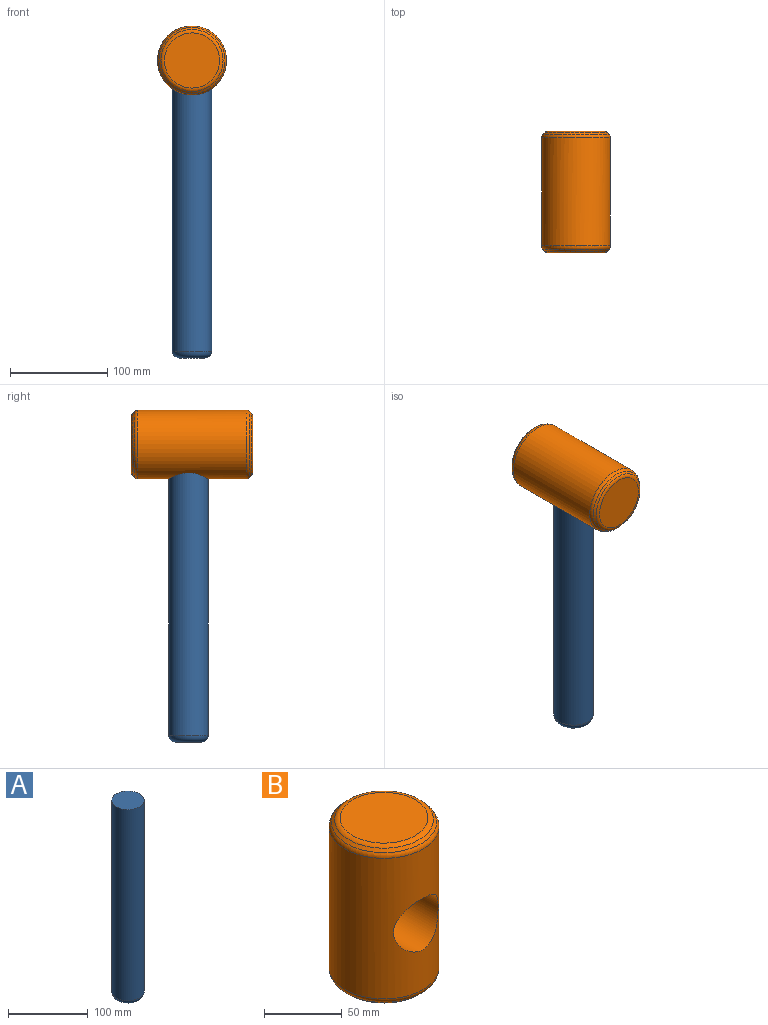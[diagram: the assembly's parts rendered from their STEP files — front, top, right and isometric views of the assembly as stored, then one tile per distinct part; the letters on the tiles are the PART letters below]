
ASSEMBLY  parts=2 mates=1
PART A: 4 faces, bbox 43.7x43.7x300 mm
  f0: cylinder r=20.2mm len=293mm, axis (0,0,-1), area 37190.6mm2, adj f1,f3
  f1: plane 40.4x40.4mm, normal (0,0,1), area 1282.1mm2, adj f0
  f2: plane 26.4x26.4mm, normal (0,0,-1), area 547.5mm2, adj f3
  f3: torus R=13.2mm, axis (0,0,1), area 1219.9mm2, adj f0,f2
PART B: 11 faces, bbox 76.6x76.6x125 mm
  f0: cylinder r=35.39mm len=110.86mm, axis (0,0,-1), area 23300.9mm2, adj f3,f8,f9
  f1: plane 56.64x56.64mm, normal (0,0,-1), area 2519.6mm2, adj f7
  f2: plane 56.64x56.64mm, normal (0,0,1), area 2519.6mm2, adj f10
  f3: cylinder r=20.3mm len=60.39mm, axis (0,1,0), area 7305.7mm2, adj f0,f4
  f4: plane 40.61x40.61mm, normal (0,-1,0), area 1295mm2, adj f3
  f5: cone r=30.39mm half-angle=45deg, axis (0,0,-1), area 605.3mm2, adj f8,f10
  f6: cone r=35.39mm half-angle=45deg, axis (0,0,1), area 605.3mm2, adj f7,f9
  f7: torus R=28.32mm, axis (0,0,1), area 744.8mm2, adj f1,f6
  f8: torus R=30.39mm, axis (0,0,1), area 860.9mm2, adj f0,f5
  f9: torus R=30.39mm, axis (0,0,-1), area 860.9mm2, adj f0,f6
  f10: torus R=28.32mm, axis (0,0,1), area 744.8mm2, adj f2,f5
PLACE A t=(-63.86,-16.18,-63.86)mm
PLACE B rot(axis=(1,0,0),90deg) t=(-63.86,42.78,241.51)mm
MATE pin_slot B.f3 <-> A.f0  axis (0,0,1) through (-63.86,-16.18,236.14)mm
